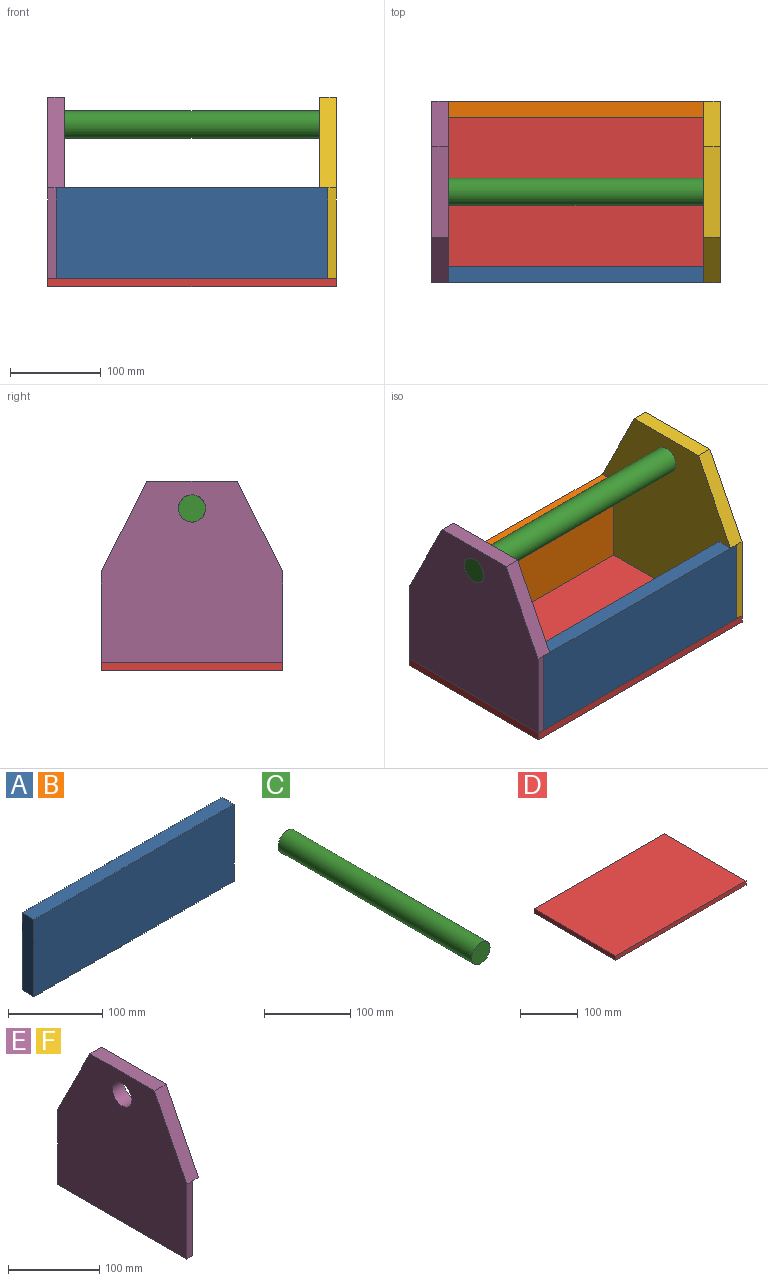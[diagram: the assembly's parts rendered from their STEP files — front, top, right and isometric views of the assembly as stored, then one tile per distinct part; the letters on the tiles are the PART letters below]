
ASSEMBLY  parts=6 mates=5
PART A: 6 faces, bbox 300x18x100 mm
  f0: plane 300x18mm, normal (0,0,-1), area 5400mm2, adj f1,f3,f4,f5
  f1: plane 100x18mm, normal (1,0,0), area 1800mm2, adj f0,f2,f4,f5
  f2: plane 300x18mm, normal (0,0,1), area 5400mm2, adj f1,f3,f4,f5
  f3: plane 100x18mm, normal (-1,0,0), area 1800mm2, adj f0,f2,f4,f5
  f4: plane 300x100mm, normal (0,-1,0), area 30000mm2, adj f0,f1,f2,f3
  f5: plane 300x100mm, normal (0,1,0), area 30000mm2, adj f0,f1,f2,f3
PART B: same geometry as A
PART C: 3 faces, bbox 30x318x30 mm
  f0: cylinder r=15mm len=318mm, axis (0,1,0), area 29970.8mm2, adj f1,f2
  f1: plane 30x30mm, normal (0,-1,0), area 706.9mm2, adj f0
  f2: plane 30x30mm, normal (0,1,0), area 706.9mm2, adj f0
PART D: 6 faces, bbox 318x200x9 mm
  f0: plane 200x9mm, normal (1,0,0), area 1800mm2, adj f1,f3,f4,f5
  f1: plane 318x9mm, normal (0,1,0), area 2862mm2, adj f0,f2,f4,f5
  f2: plane 200x9mm, normal (-1,0,0), area 1800mm2, adj f1,f3,f4,f5
  f3: plane 318x9mm, normal (0,-1,0), area 2862mm2, adj f0,f2,f4,f5
  f4: plane 318x200mm, normal (0,0,1), area 63600mm2, adj f0,f1,f2,f3
  f5: plane 318x200mm, normal (0,0,-1), area 63600mm2, adj f0,f1,f2,f3
PART E: 15 faces, bbox 18x200x200 mm
  f0: plane 100x9mm, normal (0,-1,0), area 900mm2, adj f1,f6,f8,f14
  f1: plane 200x18mm, normal (0,0,-1), area 3276mm2, adj f0,f2,f3,f8,f10,f11,f13,f14
  f2: plane 100x9mm, normal (0,1,0), area 900mm2, adj f1,f4,f8,f11
  f3: plane 200x200mm, normal (1,0,0), area 30693.1mm2, adj f1,f4,f5,f6,f7,f9,f10,f12
  f4: plane 100x50mm, normal (0,0.89,0.45), area 2012.5mm2, adj f2,f3,f5,f8,f9
  f5: plane 100x18mm, normal (0,0,1), area 1800mm2, adj f3,f4,f6,f8
  f6: plane 100x50mm, normal (0,-0.89,0.45), area 2012.5mm2, adj f0,f3,f5,f8,f12
  f7: cylinder r=15mm len=30mm, axis (-1,0,0), area 1696.5mm2, adj f3,f8
  f8: plane 200x200mm, normal (-1,0,0), area 34293.1mm2, adj f0,f1,f2,f4,f5,f6,f7
  f9: plane 18x9mm, normal (0,0,-1), area 162mm2, adj f3,f4,f10,f11
  f10: plane 100x9mm, normal (0,1,0), area 900mm2, adj f1,f3,f9,f11
  f11: plane 100x18mm, normal (1,0,0), area 1800mm2, adj f1,f2,f9,f10
  f12: plane 18x9mm, normal (0,0,-1), area 162mm2, adj f3,f6,f13,f14
  f13: plane 100x9mm, normal (0,-1,0), area 900mm2, adj f1,f3,f12,f14
  f14: plane 100x18mm, normal (1,0,0), area 1800mm2, adj f0,f1,f12,f13
PART F: same geometry as E
PLACE A rot(axis=(0,1,0),180deg) t=(47.43,-109.79,-2.86)mm
PLACE B t=(47.43,72.21,-2.86)mm
PLACE C rot(axis=(-0.58,-0.58,-0.58),120deg) t=(206.43,-27.79,117.14)mm
PLACE D t=(47.43,-27.79,-61.86)mm
PLACE E t=(-111.57,-27.79,47.14)mm
PLACE F rot(axis=(0,0,1),180deg) t=(206.43,-27.79,47.14)mm
MATE fastened B.f3 <-> E.f11  axis (-1,0,0) through (-102.57,63.21,-2.86)mm
MATE fastened F.f7 <-> C.f0  axis (1,0,0) through (206.43,-27.79,117.14)mm
MATE fastened D.f3 <-> A.f4  axis (0,-1,0) through (47.43,-127.79,-52.86)mm
MATE fastened A.f1 <-> E.f14  axis (-1,0,0) through (-102.57,-118.79,-2.86)mm
MATE fastened C.f0 <-> E.f7  axis (-1,0,0) through (-111.57,-27.79,117.14)mm
